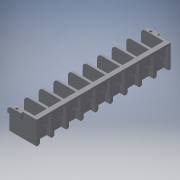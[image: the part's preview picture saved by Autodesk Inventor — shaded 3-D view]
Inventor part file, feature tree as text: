
AUTODESK INVENTOR PART (.ipt)
format: ipt  version: 2017 (Build 210142000, 142)  size: 484,352 bytes
history: native  units: in
note: dims shown in document units (in); Inventor stores cm internally (conversion verified against a paired STEP export)
features: sketch x2, other x1
ambient origin geometry x8: Origin, YZ Plane, XZ Plane, XY Plane, X Axis, Y Axis, Z Axis, Center Point
bodies: Solid1 (feature_tree)
feature tree (3):
  other  "abl2rem24150k"
  sketch  "Sketch1"
  sketch  "Sketch2"
